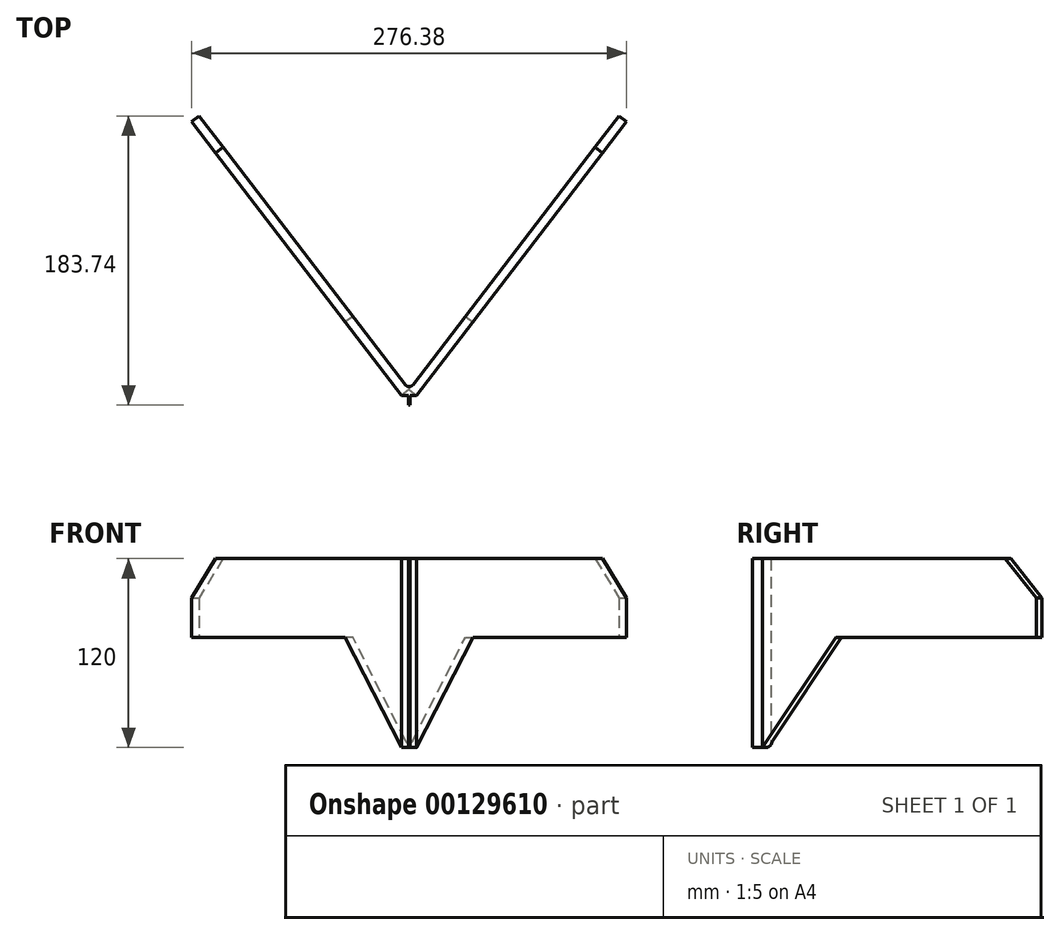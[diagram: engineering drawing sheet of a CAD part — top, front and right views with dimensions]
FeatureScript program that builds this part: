
annotation { "Feature Type Name" : "Feature", "Feature Type Description" : "" }
export const myFeature = defineFeature(function(context is Context, id is Id, definition is map)
    precondition{}
    {
        {
            var Q0;
            Q0=qCreatedBy(makeId("Top.planeOp"),FACE);
            var sketch = newSketch(context, id + "F0", { "sketchPlane" : qUnion([Q0])});
            skLineSegment(sketch, "E0", {"start": v(-138.19, 180.1) * mm, "end": v(-4.76, 6.2) * mm});
            skLineSegment(sketch, "E1", {"start": v(4.76, 6.2) * mm, "end": v(138.19, 180.1) * mm});
            skPoint(sketch, "E2.visualSharp", {"position": v(0, 0) * mm});
            skArc(sketch, "E2.filletArc", {"start": v(-4.76, 6.2) * mm, "mid": v(0, 3.86) * mm, "end": v(4.76, 6.2) * mm});
            skLineSegment(sketch, "E3", {"start": v(-138.19, 180.1) * mm, "end": v(-133.43, 183.74) * mm});
            skLineSegment(sketch, "E4", {"start": v(-133.43, 183.74) * mm, "end": v(-2.38, 12.96) * mm});
            skLineSegment(sketch, "E5", {"start": v(138.19, 180.1) * mm, "end": v(133.43, 183.74) * mm});
            skLineSegment(sketch, "E6", {"start": v(133.43, 183.74) * mm, "end": v(2.38, 12.96) * mm});
            skArc(sketch, "E7.filletArc", {"start": v(-2.38, 12.96) * mm, "mid": v(0, 11.78) * mm, "end": v(2.38, 12.96) * mm});
            skSolve(sketch);
        }
        {
            var Q0;
            Q0=qSketchRegion(id+"F0",true);
            extrude(context, id + "F1", {"entities" : qUnion([Q0]), "depth" : 50 * mm, "hasSecondDirection" : true, "secondDirectionOppositeDirection" : true, "secondDirectionDepth" : 70 * mm});
        }
        {
            var Q0;
            Q0=makeQuery(id+"F1.opExtrude","CAP_EDGE",EDGE,{"disambiguationData":[OSD([sQuery(id+"F0.wireOp",EDGE,"E3")])],"isStart":false});
            var Q1;
            Q1=makeQuery(id+"F1.opExtrude","CAP_EDGE",EDGE,{"disambiguationData":[OSD([sQuery(id+"F0.wireOp",EDGE,"E5")])],"isStart":false});
            chamfer(context, id + "F2", {"entities" : qUnion([Q0, Q1]), "width" : 25 * mm, "tangentPropagation" : true});
        }
        {
            var Q0;
            Q0=makeQuery(id+"F1.opExtrude","SWEPT_FACE",FACE,{"disambiguationData":[OSD([sQuery(id+"F0.wireOp",EDGE,"E0")])]});
            var sketch = newSketch(context, id + "F3", { "sketchPlane" : qUnion([Q0])});
            skLineSegment(sketch, "E8", {"start": v(-227, 0) * mm, "end": v(-66.56, 0) * mm});
            skLineSegment(sketch, "E9", {"start": v(-66.56, 0) * mm, "end": v(-7.82, -70) * mm});
            skLineSegment(sketch, "E10.0", {"start": v(-227, -70) * mm, "end": v(-7.82, -70) * mm});
            skLineSegment(sketch, "E11.0", {"start": v(-227, 0) * mm, "end": v(-227, -70) * mm});
            skSolve(sketch);
        }
        {
            var Q0;
            Q0=qSketchRegion(id+"F3",true);
            extrude(context, id + "F4", {"entities" : qUnion([Q0]), "operationType" : NewBodyOperationType.REMOVE, "oppositeDirection" : true, "depth" : 25 * mm});
        }
        {
            var Q0;
            Q0=makeQuery(id+"F1.opExtrude","SWEPT_FACE",FACE,{"disambiguationData":[OSD([sQuery(id+"F0.wireOp",EDGE,"E1")])]});
            var sketch = newSketch(context, id + "F5", { "sketchPlane" : qUnion([Q0])});
            skLineSegment(sketch, "E12", {"start": v(7.82, -70) * mm, "end": v(66.56, 0) * mm});
            skLineSegment(sketch, "E13", {"start": v(66.56, 0) * mm, "end": v(227, 0) * mm});
            skLineSegment(sketch, "E14.0", {"start": v(7.82, -70) * mm, "end": v(227, -70) * mm});
            skLineSegment(sketch, "E15.0", {"start": v(227, 0) * mm, "end": v(227, -70) * mm});
            skPoint(sketch, "E16.orphan", {"position": v(227, 25) * mm});
            skSolve(sketch);
        }
        {
            var Q0;
            Q0=qSketchRegion(id+"F5",true);
            extrude(context, id + "F6", {"entities" : qUnion([Q0]), "operationType" : NewBodyOperationType.REMOVE, "oppositeDirection" : true, "depth" : 25 * mm});
        }
        {
            var Q0;
            Q0=qCreatedBy(makeId("Top.planeOp"),FACE);
            var sketch = newSketch(context, id + "F7", { "sketchPlane" : qUnion([Q0])});
            skLineSegment(sketch, "E17.top", {"start": v(-4.76, 0) * mm, "end": v(4.74, 0) * mm});
            skLineSegment(sketch, "E17.left", {"start": v(-4.76, 6.2) * mm, "end": v(-4.76, 0) * mm});
            skLineSegment(sketch, "E17.right", {"start": v(4.74, 6.2) * mm, "end": v(4.74, 0) * mm});
            skLineSegment(sketch, "E18", {"start": v(-4.76, 6.2) * mm, "end": v(4.76, 6.2) * mm});
            skSolve(sketch);
        }
        {
            var Q0;
            Q0=makeQuery(id+"F7.imprint","IMPRINT",FACE,{"disambiguationData":[TD([[makeQuery(id+"F7.imprint","IMPRINT",EDGE,{"derivedFrom":sQuery(id+"F7.wireOp",EDGE,"E17.top")}),1.0]])]});
            extrude(context, id + "F8", {"entities" : qUnion([Q0]), "operationType" : NewBodyOperationType.REMOVE, "depth" : 150 * mm, "hasSecondDirection" : true, "secondDirectionOppositeDirection" : true, "secondDirectionDepth" : 150 * mm});
        }
        {
            var Q0;
            Q0=qCreatedBy(makeId("Right.planeOp"),FACE);
            var sketch = newSketch(context, id + "F9", { "sketchPlane" : qUnion([Q0])});
            skLineSegment(sketch, "E19.bottom", {"start": v(6.2, 50) * mm, "end": v(0, 50) * mm});
            skLineSegment(sketch, "E19.top", {"start": v(6.2, -70) * mm, "end": v(0, -70) * mm});
            skLineSegment(sketch, "E19.left", {"start": v(6.2, 50) * mm, "end": v(6.2, -70) * mm});
            skLineSegment(sketch, "E19.right", {"start": v(0, 50) * mm, "end": v(0, -70) * mm});
            skSolve(sketch);
        }
        {
            var Q0;
            Q0=qSketchRegion(id+"F9",true);
            extrude(context, id + "F10", {"entities" : qUnion([Q0]), "operationType" : NewBodyOperationType.ADD, "endBound" : BoundingType.SYMMETRIC, "depth" : 1 * mm});
        }
    });
